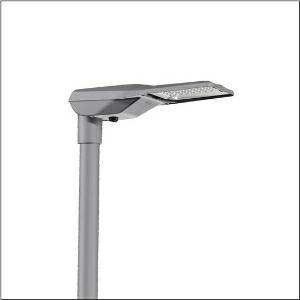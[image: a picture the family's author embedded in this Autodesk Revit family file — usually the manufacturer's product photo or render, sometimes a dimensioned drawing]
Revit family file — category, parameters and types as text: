
# Revit family: streetlight_sl_21_mini___p0_8ab_5xe2r33r08gb_1b3d
name_source: partatom
category: Lighting Fixtures
units: mm (PartAtom-declared; Revit-internal decimal feet)

## family parameters
Cut with Voids When Loaded = No
Host = Face
Light Source = No
Part Type = Normal
Room Calculation Point = No
Round Connector Dimension = Use Diameter
Shared = No

## types (1)
- --- (1 x LED, 5160 lm, 40.4 W, 3000K)
    Apparent Load = 40 VA
    CIE Flux Codes = 36 71 98 100 100
    Color Rendering = 70
    Color Temperature = 3000K
    Default Elevation = 1800 mm
    Description = Streetlight SL 21 mini, mast luminaire, primary light control with lens, of PMMA, primary optical cover: cover, of toughened safety glass, transparent, light distribution: P0.8aB, light emission: direct distribution, primary light characteristic: asymmetric, installation type: post-top, side-entry, LED, High Power LED, rated luminous flux: 5.160lm, luminous efficacy: 128lm/W, light colour: 730, colour temperature: 3000K, control gear: D4i, control: pre-setting: logarithmic dimming characteristic, flexible luminous flux parameterisation, time-dependent luminous flux control, constant luminous flux control, overheat protection, mains connection: 220..240V, AC, 50/60Hz, start of lifetime: 40W, end of service life: 41W, reduction: 19W, luminaire housing, of diecast aluminium, powder-coated, Siteco® metallic grey (DB 702S), corrosivity category C5 mid according to DIN EN ISO 12944, multi-level sealing system, sealing non-destructively replaceable, inclination adjustable: 0°, 5°, 10°, 15°, please order mast flange separately, length: 628mm, width: 235mm, height: 110mm, mast flange for spigot size: 42mm (side-entry): 5XC10008XM4, 60/48mm (side-entry/post-top): 5XC10108XM2, 76/60mm (side-entry/post-top): 5XC10108XM1, mounting height: 4..8m, Smart Interface below, protection rating (complete): IP66, insulation class (complete): insulation class II (safety insulation), certification: CE, ENEC, ENEC+, VDE, impact resistance: IK10, permissible operating ambient temperature for outdoor applications: -40..+50°C, standard-compliant lighting for roads and squares, packaging unit: 1 piece

Light Distribution: P0.8aB
    Height = 110 mm
    Lamp = 1 x LED
    Lamp Light Flux = 5160 lm
    Lamp Power = 40.4 W
    Lamp count = 1
    Length = 625 mm
    Luminous efficacy = 128 lm/W
    Manufacturer = Siteco
    ModVariant = No
    Model = 5XE2R33R08GB
    Number of Poles = 1
    OnlyDefault = Yes
    Power Factor = 1
    Product Name = Streetlight SL 21 mini | P0.8aB
    Product group = mast luminaire | pylon top
    ProductGroupID = 6100
    Protection Class = Protection class II
    Protection Degree = IP 66
    RLX_Detail_Level = 1
    RLX_Emergency_Light_Flux = 0 lm
    RLX_Emergency_Type = 0
    RLX_Emergency_Type_DB = No
    RlxData = <blob elided: 25881 chars, md5=32c321dd>
    Socket = socket
    Standby Power = 0 W
    System Light Flux = 5160 lm
    System Power = 40 W
    Type Comments = factory setting: luminous flux: 100 % | dim-lin: 254 | 812 mA
    Type Image = l_1003516.jpg
    URL = http://relux.com
    VarID = @adj_074674
    Voltage = 0 V
    Weight = 0.00 kg
    Width = 234 mm

## geometry (parser evidence)
native form markers: Blend x4, Sweep x13
no freeform markers — native parametric forms only
